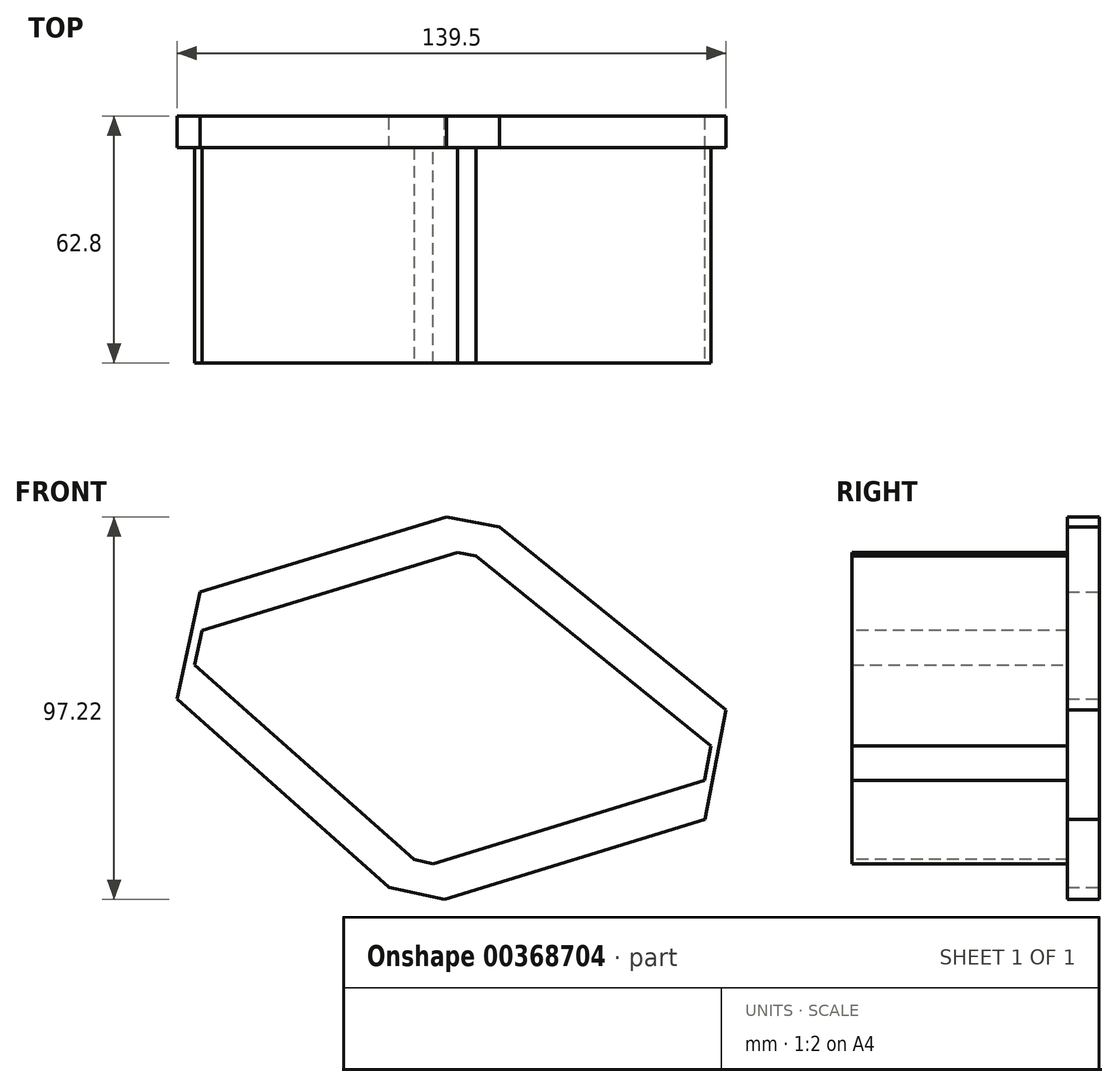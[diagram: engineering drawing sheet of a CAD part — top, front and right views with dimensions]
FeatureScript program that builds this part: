
annotation { "Feature Type Name" : "Feature", "Feature Type Description" : "" }
export const myFeature = defineFeature(function(context is Context, id is Id, definition is map)
    precondition{}
    {
        {
            var Q0;
            Q0=qCreatedBy(makeId("Front.planeOp"),FACE);
            var sketch = newSketch(context, id + "F0", { "sketchPlane" : qUnion([Q0])});
            skLineSegment(sketch, "E0", {"start": v(0, 0) * mm, "end": v(-64.65, 57.38) * mm});
            skLineSegment(sketch, "E1", {"start": v(-64.65, 57.38) * mm, "end": v(11.44, 80.67) * mm});
            skLineSegment(sketch, "E2", {"start": v(11.44, 80.67) * mm, "end": v(80.71, 24.75) * mm});
            skLineSegment(sketch, "E3", {"start": v(80.71, 24.75) * mm, "end": v(0, 0) * mm});
            skSolve(sketch);
        }
        {
            var Q0;
            Q0=makeQuery(id+"F0.imprint","IMPRINT",FACE,{"disambiguationData":[TD([[makeQuery(id+"F0.imprint","IMPRINT",EDGE,{"derivedFrom":sQuery(id+"F0.wireOp",EDGE,"E0")}),-1.0]])]});
            extrude(context, id + "F1", {"entities" : qUnion([Q0]), "oppositeDirection" : true, "depth" : 62.8 * mm});
        }
        {
            var Q0;
            Q0=makeQuery(id+"F1.opExtrude","SWEPT_EDGE",EDGE,{"disambiguationData":[OSD([sQuery(id+"F0.wireOp",EDGE,"E1"),sQuery(id+"F0.wireOp",EDGE,"E2")])]});
            var Q1;
            Q1=makeQuery(id+"F1.opExtrude","SWEPT_EDGE",EDGE,{"disambiguationData":[OSD([sQuery(id+"F0.wireOp",EDGE,"E2"),sQuery(id+"F0.wireOp",EDGE,"E3")])]});
            var Q2;
            Q2=makeQuery(id+"F1.opExtrude","SWEPT_EDGE",EDGE,{"disambiguationData":[OSD([sQuery(id+"F0.wireOp",EDGE,"E0"),sQuery(id+"F0.wireOp",EDGE,"E1")])]});
            var Q3;
            Q3=makeQuery(id+"F1.opExtrude","SWEPT_EDGE",EDGE,{"disambiguationData":[OSD([sQuery(id+"F0.wireOp",EDGE,"E0"),sQuery(id+"F0.wireOp",EDGE,"E3")])]});
            chamfer(context, id + "F2", {"entities" : qUnion([Q0, Q1, Q2, Q3]), "width" : 5.08 * mm, "tangentPropagation" : true});
        }
        {
            var Q0;
            Q0=makeQuery(id+"F1.opExtrude","CAP_FACE",FACE,{"disambiguationData":[OSD([sQuery(id+"F0.wireOp",EDGE,"E0"),sQuery(id+"F0.wireOp",EDGE,"E1"),sQuery(id+"F0.wireOp",EDGE,"E2"),sQuery(id+"F0.wireOp",EDGE,"E3")])],"isStart":false});
            var sketch = newSketch(context, id + "F3", { "sketchPlane" : qUnion([Q0])});
            skLineSegment(sketch, "E4.0", {"start": v(56.46, 69.83) * mm, "end": v(62.38, 42.65) * mm});
            skLineSegment(sketch, "E4.1", {"start": v(-6.06, 88.97) * mm, "end": v(56.46, 69.83) * mm});
            skLineSegment(sketch, "E4.2", {"start": v(62.38, 42.65) * mm, "end": v(8.47, -5.2) * mm});
            skLineSegment(sketch, "E4.3", {"start": v(-19.52, 86.37) * mm, "end": v(-6.06, 88.97) * mm});
            skLineSegment(sketch, "E4.4", {"start": v(8.47, -5.2) * mm, "end": v(-5.55, -8.25) * mm});
            skLineSegment(sketch, "E4.5", {"start": v(-5.55, -8.25) * mm, "end": v(-71.75, 12.05) * mm});
            skLineSegment(sketch, "E4.6", {"start": v(-71.75, 12.05) * mm, "end": v(-77.12, 39.87) * mm});
            skLineSegment(sketch, "E4.7", {"start": v(-77.12, 39.87) * mm, "end": v(-19.52, 86.37) * mm});
            skSolve(sketch);
        }
        {
            var Q0;
            Q0=makeQuery(id+"F3.imprint","IMPRINT",FACE,{"disambiguationData":[TD([[makeQuery(id+"F3.imprint","IMPRINT",EDGE,{"derivedFrom":sQuery(id+"F3.wireOp",EDGE,"E4.0")}),-1.0]])]});
            extrude(context, id + "F4", {"entities" : qUnion([Q0]), "operationType" : NewBodyOperationType.ADD, "oppositeDirection" : true, "depth" : 8.03 * mm});
        }
    });
